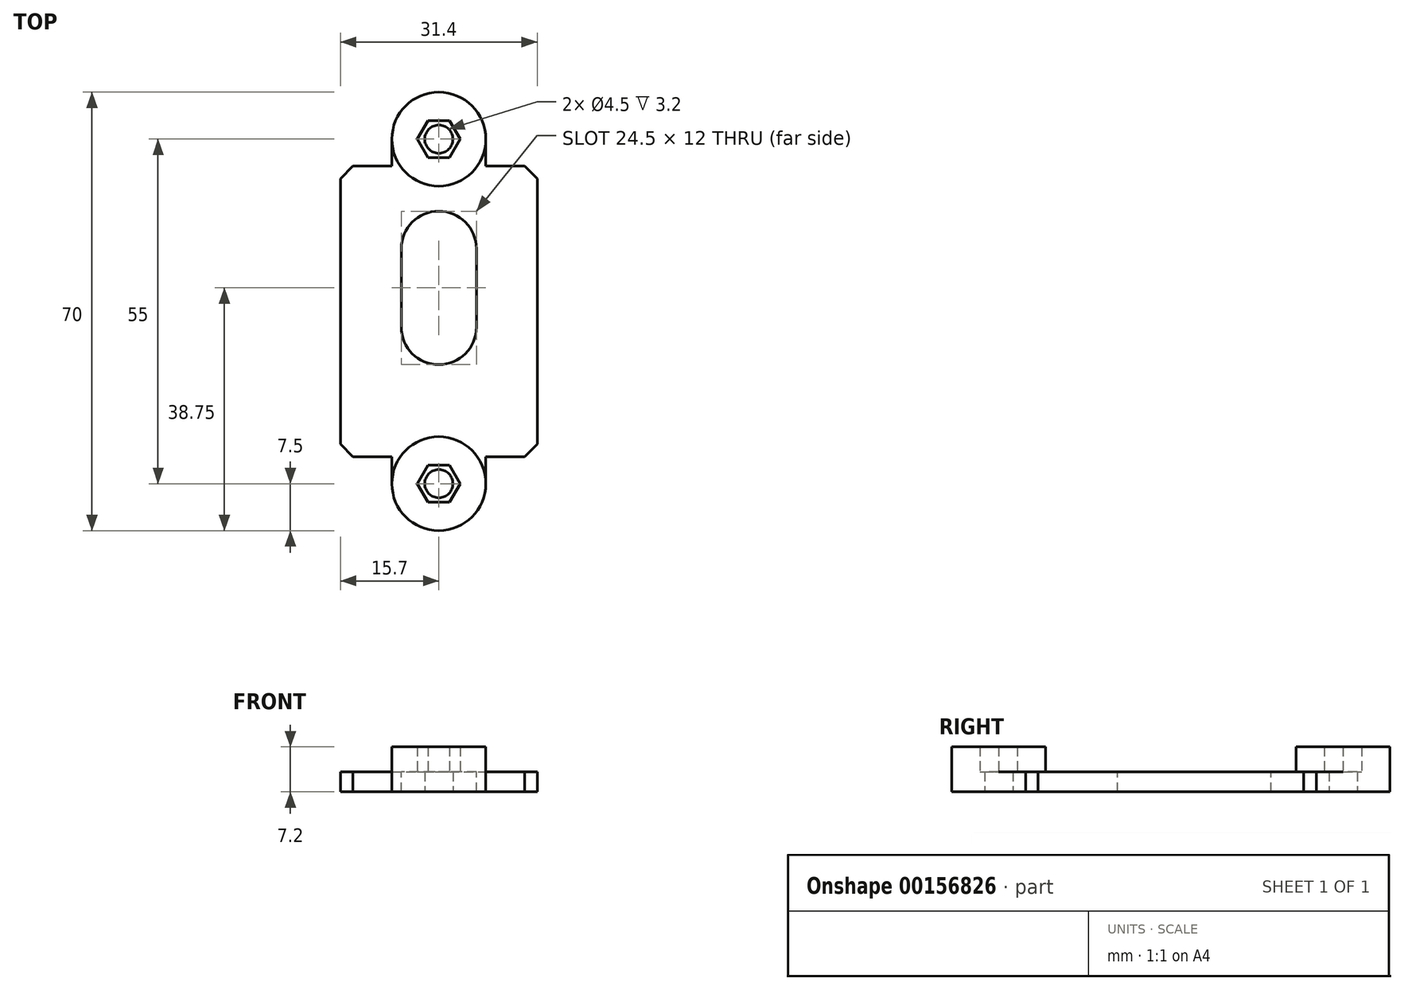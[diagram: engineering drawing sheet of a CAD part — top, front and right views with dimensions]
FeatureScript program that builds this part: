
annotation { "Feature Type Name" : "Feature", "Feature Type Description" : "" }
export const myFeature = defineFeature(function(context is Context, id is Id, definition is map)
    precondition{}
    {
        {
            var Q0;
            Q0=qCreatedBy(makeId("Top.planeOp"),FACE);
            var sketch = newSketch(context, id + "F0", { "sketchPlane" : qUnion([Q0])});
            skLineSegment(sketch, "E0.rect.bottom", {"start": v(12.5, -20) * mm, "end": v(-12.5, -20) * mm});
            skLineSegment(sketch, "E0.rect.top", {"start": v(12.5, 20) * mm, "end": v(-12.5, 20) * mm});
            skLineSegment(sketch, "E0.rect.left", {"start": v(12.5, -20) * mm, "end": v(12.5, 20) * mm});
            skLineSegment(sketch, "E0.rect.right", {"start": v(-12.5, -20) * mm, "end": v(-12.5, 20) * mm});
            skPoint(sketch, "E0.rect.middle", {"position": v(0, 0) * mm});
            skCircle(sketch, "E1", {"center": v(0, 0) * mm, "radius": 6.25 * mm});
            skSolve(sketch);
        }
        {
            var Q0;
            Q0=qSketchRegion(id+"F0",true);
            extrude(context, id + "F1", {"entities" : qUnion([Q0]), "depth" : 3.2 * mm});
        }
        {
            var Q0;
            Q0=makeQuery(id+"F1.opExtrude","CAP_FACE",FACE,{"disambiguationData":[OSD([sQuery(id+"F0.wireOp",EDGE,"E0.rect.bottom"),sQuery(id+"F0.wireOp",EDGE,"E0.rect.top"),sQuery(id+"F0.wireOp",EDGE,"E0.rect.left"),sQuery(id+"F0.wireOp",EDGE,"E0.rect.right"),sQuery(id+"F0.wireOp",EDGE,"E1")])],"isStart":false});
            var sketch = newSketch(context, id + "F2", { "sketchPlane" : qUnion([Q0])});
            skLineSegment(sketch, "E2.rect.bottom", {"start": v(12.5, 20) * mm, "end": v(-12.5, 20) * mm});
            skLineSegment(sketch, "E2.rect.top", {"start": v(12.5, -20) * mm, "end": v(-12.5, -20) * mm});
            skLineSegment(sketch, "E2.rect.left", {"start": v(12.5, 20) * mm, "end": v(12.5, -20) * mm});
            skLineSegment(sketch, "E2.rect.right", {"start": v(-12.5, 20) * mm, "end": v(-12.5, -20) * mm});
            skPoint(sketch, "E2.rect.middle", {"position": v(0, 0) * mm});
            skLineSegment(sketch, "E3.rect.bottom", {"start": v(15.7, 23.2) * mm, "end": v(7.5, 23.2) * mm});
            skLineSegment(sketch, "E3.rect.left", {"start": v(15.7, 23.2) * mm, "end": v(15.7, -23.2) * mm});
            skLineSegment(sketch, "E3.rect.right", {"start": v(-15.7, 23.2) * mm, "end": v(-15.7, -23.2) * mm});
            skLineSegment(sketch, "E4", {"start": v(-7.5, 23.2) * mm, "end": v(-7.5, 27.5) * mm});
            skLineSegment(sketch, "E5", {"start": v(0, 27.5) * mm, "end": v(0, 23.2) * mm, "construction": true});
            skLineSegment(sketch, "E6", {"start": v(0, 0) * mm, "end": v(-6.25, 0) * mm, "construction": true});
            skLineSegment(sketch, "E7.MirrorCS", {"start": v(7.5, 23.2) * mm, "end": v(7.5, 27.5) * mm});
            skArc(sketch, "E8", {"start": v(-7.5, 27.5) * mm, "mid": v(0, 35) * mm, "end": v(7.5, 27.5) * mm});
            skLineSegment(sketch, "E9.MirrorCS", {"start": v(-7.5, -23.2) * mm, "end": v(-7.5, -27.5) * mm});
            skLineSegment(sketch, "E10.MirrorCS", {"start": v(15.7, -23.2) * mm, "end": v(7.5, -23.2) * mm});
            skLineSegment(sketch, "E11.MirrorCS", {"start": v(0, -27.5) * mm, "end": v(0, -23.2) * mm, "construction": true});
            skArc(sketch, "E12.MirrorCS", {"start": v(-7.5, -27.5) * mm, "mid": v(0, -35) * mm, "end": v(7.5, -27.5) * mm});
            skLineSegment(sketch, "E13.MirrorCS", {"start": v(7.5, -23.2) * mm, "end": v(7.5, -27.5) * mm});
            skLineSegment(sketch, "E14.trimOffspring", {"start": v(-7.5, -23.2) * mm, "end": v(-15.7, -23.2) * mm});
            skLineSegment(sketch, "E15.trimOffspring", {"start": v(-7.5, 23.2) * mm, "end": v(-15.7, 23.2) * mm});
            skCircle(sketch, "E16.cCircle", {"center": v(0, 27.5) * mm, "radius": 2.98 * mm, "construction": true});
            skLineSegment(sketch, "E16.0", {"start": v(-1.72, 30.48) * mm, "end": v(1.72, 30.48) * mm});
            skLineSegment(sketch, "E16.1", {"start": v(1.72, 30.48) * mm, "end": v(3.44, 27.5) * mm});
            skLineSegment(sketch, "E16.2", {"start": v(3.44, 27.5) * mm, "end": v(1.72, 24.52) * mm});
            skLineSegment(sketch, "E16.3", {"start": v(1.72, 24.52) * mm, "end": v(-1.72, 24.52) * mm});
            skLineSegment(sketch, "E16.4", {"start": v(-1.72, 24.52) * mm, "end": v(-3.44, 27.5) * mm});
            skLineSegment(sketch, "E16.5", {"start": v(-3.44, 27.5) * mm, "end": v(-1.72, 30.48) * mm});
            skPoint(sketch, "E16.0.midPoint", {"position": v(0, 30.48) * mm});
            skCircle(sketch, "E17.cCircle", {"center": v(0, -27.5) * mm, "radius": 2.98 * mm, "construction": true});
            skLineSegment(sketch, "E17.0", {"start": v(-1.72, -24.52) * mm, "end": v(1.72, -24.52) * mm});
            skLineSegment(sketch, "E17.1", {"start": v(1.72, -24.52) * mm, "end": v(3.44, -27.5) * mm});
            skLineSegment(sketch, "E17.2", {"start": v(3.44, -27.5) * mm, "end": v(1.72, -30.47) * mm});
            skLineSegment(sketch, "E17.3", {"start": v(1.72, -30.48) * mm, "end": v(-1.72, -30.48) * mm});
            skLineSegment(sketch, "E17.4", {"start": v(-1.72, -30.48) * mm, "end": v(-3.44, -27.5) * mm});
            skLineSegment(sketch, "E17.5", {"start": v(-3.44, -27.5) * mm, "end": v(-1.72, -24.52) * mm});
            skPoint(sketch, "E17.0.midPoint", {"position": v(0, -24.52) * mm});
            skSolve(sketch);
        }
        {
            var Q0;
            Q0=qSketchRegion(id+"F2",true);
            extrude(context, id + "F3", {"entities" : qUnion([Q0]), "operationType" : NewBodyOperationType.ADD, "oppositeDirection" : true, "depth" : 40 * mm});
        }
        {
            var Q0;
            Q0=makeQuery(id+"F3.boolean.opBoolean","MERGE",FACE,{"derivedFrom":[makeQuery(id+"F1.opExtrude","CAP_FACE",FACE,{"disambiguationData":[OSD([sQuery(id+"F0.wireOp",EDGE,"E0.rect.bottom"),sQuery(id+"F0.wireOp",EDGE,"E0.rect.top"),sQuery(id+"F0.wireOp",EDGE,"E0.rect.left"),sQuery(id+"F0.wireOp",EDGE,"E0.rect.right"),sQuery(id+"F0.wireOp",EDGE,"E1")])],"isStart":false}),makeQuery(id+"F3.opExtrude","CAP_FACE",FACE,{"disambiguationData":[OSD([sQuery(id+"F2.wireOp",EDGE,"E2.rect.bottom"),sQuery(id+"F2.wireOp",EDGE,"E2.rect.top"),sQuery(id+"F2.wireOp",EDGE,"E2.rect.left"),sQuery(id+"F2.wireOp",EDGE,"E2.rect.right"),sQuery(id+"F2.wireOp",EDGE,"E3.rect.bottom"),sQuery(id+"F2.wireOp",EDGE,"E3.rect.top"),sQuery(id+"F2.wireOp",EDGE,"E3.rect.left"),sQuery(id+"F2.wireOp",EDGE,"E3.rect.right")])],"isStart":true})]});
            var sketch = newSketch(context, id + "F4", { "sketchPlane" : qUnion([Q0])});
            skLineSegment(sketch, "E18", {"start": v(-15.7, 23.2) * mm, "end": v(-30.7, 23.2) * mm});
            skLineSegment(sketch, "E19", {"start": v(-30.7, 23.2) * mm, "end": v(-30.7, -23.2) * mm});
            skLineSegment(sketch, "E20", {"start": v(-30.7, -23.2) * mm, "end": v(-15.7, -23.2) * mm});
            skLineSegment(sketch, "E21", {"start": v(-15.7, -23.2) * mm, "end": v(-15.7, 23.2) * mm});
            skCircle(sketch, "E22", {"center": v(-23.2, 13.2) * mm, "radius": 2.25 * mm});
            skCircle(sketch, "E23", {"center": v(-23.2, -13.2) * mm, "radius": 2.25 * mm});
            skPoint(sketch, "E23.centerSnap0", {"position": v(-23.2, -23.2) * mm});
            skSolve(sketch);
        }
        {
            var Q0;
            Q0=qSketchRegion(id+"F4",true);
            extrude(context, id + "F5", {"entities" : qUnion([Q0]), "operationType" : NewBodyOperationType.ADD, "oppositeDirection" : true, "depth" : 5 * mm});
        }
        {
            var Q0;
            Q0=makeQuery(id+"F3.opExtrude","SWEPT_EDGE",EDGE,{"disambiguationData":[OSD([sQuery(id+"F2.wireOp",EDGE,"E3.rect.bottom"),sQuery(id+"F2.wireOp",EDGE,"E3.rect.left")])]});
            var Q1;
            Q1=makeQuery(id+"F3.opExtrude","SWEPT_EDGE",EDGE,{"disambiguationData":[OSD([sQuery(id+"F2.wireOp",EDGE,"E3.rect.right"),sQuery(id+"F2.wireOp",EDGE,"E15.trimOffspring")])]});
            var Q2;
            Q2=makeQuery(id+"F3.opExtrude","SWEPT_EDGE",EDGE,{"disambiguationData":[OSD([sQuery(id+"F2.wireOp",EDGE,"E3.rect.right"),sQuery(id+"F2.wireOp",EDGE,"E14.trimOffspring")])]});
            var Q3;
            Q3=makeQuery(id+"F3.opExtrude","SWEPT_EDGE",EDGE,{"disambiguationData":[OSD([sQuery(id+"F2.wireOp",EDGE,"E3.rect.bottom"),sQuery(id+"F2.wireOp",EDGE,"E3.rect.left")])]});
            var Q4;
            Q4=makeQuery(id+"F3.opExtrude","SWEPT_EDGE",EDGE,{"disambiguationData":[OSD([sQuery(id+"F2.wireOp",EDGE,"E3.rect.bottom"),sQuery(id+"F2.wireOp",EDGE,"E3.rect.left")])]});
            var Q5;
            Q5=makeQuery(id+"F3.opExtrude","SWEPT_EDGE",EDGE,{"disambiguationData":[OSD([sQuery(id+"F2.wireOp",EDGE,"E3.rect.left"),sQuery(id+"F2.wireOp",EDGE,"E10.MirrorCS")])]});
            var Q6;
            Q6=makeQuery(id+"F3.opExtrude","SWEPT_EDGE",EDGE,{"disambiguationData":[OSD([sQuery(id+"F2.wireOp",EDGE,"E3.rect.right"),sQuery(id+"F2.wireOp",EDGE,"E15.trimOffspring")])]});
            var Q7;
            Q7=makeQuery(id+"F3.opExtrude","SWEPT_EDGE",EDGE,{"disambiguationData":[OSD([sQuery(id+"F2.wireOp",EDGE,"E3.rect.right"),sQuery(id+"F2.wireOp",EDGE,"E14.trimOffspring")])]});
            var Q8;
            Q8=makeQuery(id+"F5.opExtrude","SWEPT_EDGE",EDGE,{"disambiguationData":[OSD([sQuery(id+"F4.wireOp",EDGE,"E18"),sQuery(id+"F4.wireOp",EDGE,"E19")])]});
            var Q9;
            Q9=makeQuery(id+"F5.opExtrude","SWEPT_EDGE",EDGE,{"disambiguationData":[OSD([sQuery(id+"F4.wireOp",EDGE,"E19"),sQuery(id+"F4.wireOp",EDGE,"E20")])]});
            chamfer(context, id + "F6", {"entities" : qUnion([Q0, Q1, Q2, Q3, Q4, Q5, Q6, Q7, Q8, Q9]), "width" : 2 * mm, "tangentPropagation" : true});
        }
        {
            var Q0;
            Q0=makeQuery(id+"F3.opExtrude","CAP_FACE",FACE,{"disambiguationData":[OSD([sQuery(id+"F2.wireOp",EDGE,"E2.rect.bottom"),sQuery(id+"F2.wireOp",EDGE,"E2.rect.top"),sQuery(id+"F2.wireOp",EDGE,"E2.rect.left"),sQuery(id+"F2.wireOp",EDGE,"E2.rect.right"),sQuery(id+"F2.wireOp",EDGE,"E3.rect.bottom"),sQuery(id+"F2.wireOp",EDGE,"E3.rect.left"),sQuery(id+"F2.wireOp",EDGE,"E3.rect.right"),sQuery(id+"F2.wireOp",EDGE,"E4"),sQuery(id+"F2.wireOp",EDGE,"E7.MirrorCS"),sQuery(id+"F2.wireOp",EDGE,"E8"),sQuery(id+"F2.wireOp",EDGE,"E9.MirrorCS"),sQuery(id+"F2.wireOp",EDGE,"E10.MirrorCS"),sQuery(id+"F2.wireOp",EDGE,"E12.MirrorCS"),sQuery(id+"F2.wireOp",EDGE,"E13.MirrorCS"),sQuery(id+"F2.wireOp",EDGE,"E14.trimOffspring"),sQuery(id+"F2.wireOp",EDGE,"E15.trimOffspring"),sQuery(id+"F2.wireOp",EDGE,"E16.0"),sQuery(id+"F2.wireOp",EDGE,"E16.1"),sQuery(id+"F2.wireOp",EDGE,"E16.2"),sQuery(id+"F2.wireOp",EDGE,"E16.3"),sQuery(id+"F2.wireOp",EDGE,"E16.4"),sQuery(id+"F2.wireOp",EDGE,"E16.5"),sQuery(id+"F2.wireOp",EDGE,"E17.0"),sQuery(id+"F2.wireOp",EDGE,"E17.1"),sQuery(id+"F2.wireOp",EDGE,"E17.2"),sQuery(id+"F2.wireOp",EDGE,"E17.3"),sQuery(id+"F2.wireOp",EDGE,"E17.4"),sQuery(id+"F2.wireOp",EDGE,"E17.5")])],"isStart":false});
            var sketch = newSketch(context, id + "F7", { "sketchPlane" : qUnion([Q0])});
            skCircle(sketch, "E24.cCircle", {"center": v(0, 27.5) * mm, "radius": 2.98 * mm, "construction": true});
            skLineSegment(sketch, "E24.0", {"start": v(-1.72, 30.48) * mm, "end": v(1.72, 30.47) * mm});
            skLineSegment(sketch, "E24.1", {"start": v(1.72, 30.47) * mm, "end": v(3.44, 27.5) * mm});
            skLineSegment(sketch, "E24.2", {"start": v(3.44, 27.5) * mm, "end": v(1.72, 24.52) * mm});
            skLineSegment(sketch, "E24.3", {"start": v(1.72, 24.52) * mm, "end": v(-1.72, 24.53) * mm});
            skLineSegment(sketch, "E24.4", {"start": v(-1.72, 24.53) * mm, "end": v(-3.44, 27.5) * mm});
            skLineSegment(sketch, "E24.5", {"start": v(-3.44, 27.5) * mm, "end": v(-1.72, 30.48) * mm});
            skPoint(sketch, "E24.0.midPoint", {"position": v(0, 30.48) * mm});
            skLineSegment(sketch, "E25", {"start": v(0, 0) * mm, "end": v(12.5, 0) * mm, "construction": true});
            skCircle(sketch, "E26", {"center": v(0, 27.5) * mm, "radius": 2.25 * mm});
            skLineSegment(sketch, "E27.MirrorCS", {"start": v(-1.72, -30.48) * mm, "end": v(1.72, -30.47) * mm});
            skCircle(sketch, "E28.MirrorC", {"center": v(0, -27.5) * mm, "radius": 2.98 * mm, "construction": true});
            skLineSegment(sketch, "E29.MirrorCS", {"start": v(1.72, -30.47) * mm, "end": v(3.44, -27.5) * mm});
            skLineSegment(sketch, "E30.MirrorCS", {"start": v(3.44, -27.5) * mm, "end": v(1.72, -24.52) * mm});
            skLineSegment(sketch, "E31.MirrorCS", {"start": v(1.72, -24.52) * mm, "end": v(-1.72, -24.53) * mm});
            skLineSegment(sketch, "E32.MirrorCS", {"start": v(-1.72, -24.53) * mm, "end": v(-3.44, -27.5) * mm});
            skLineSegment(sketch, "E33.MirrorCS", {"start": v(-3.44, -27.5) * mm, "end": v(-1.72, -30.48) * mm});
            skCircle(sketch, "E34.MirrorC", {"center": v(0, -27.5) * mm, "radius": 2.25 * mm});
            skPoint(sketch, "E35.MirrorP", {"position": v(0, -30.48) * mm});
            skSolve(sketch);
        }
        {
            var Q0;
            Q0=qSketchRegion(id+"F7",true);
            extrude(context, id + "F8", {"entities" : qUnion([Q0]), "operationType" : NewBodyOperationType.ADD, "oppositeDirection" : true, "depth" : 3.2 * mm});
        }
        {
            var Q0;
            Q0=makeQuery(id+"F5.boolean.opBoolean","MERGE",FACE,{"derivedFrom":[makeQuery(id+"F3.boolean.opBoolean","MERGE",FACE,{"derivedFrom":[makeQuery(id+"F1.opExtrude","CAP_FACE",FACE,{"disambiguationData":[OSD([sQuery(id+"F0.wireOp",EDGE,"E0.rect.bottom"),sQuery(id+"F0.wireOp",EDGE,"E0.rect.top"),sQuery(id+"F0.wireOp",EDGE,"E0.rect.left"),sQuery(id+"F0.wireOp",EDGE,"E0.rect.right"),sQuery(id+"F0.wireOp",EDGE,"E1")])],"isStart":false}),makeQuery(id+"F3.opExtrude","CAP_FACE",FACE,{"disambiguationData":[OSD([sQuery(id+"F2.wireOp",EDGE,"E2.rect.bottom"),sQuery(id+"F2.wireOp",EDGE,"E2.rect.top"),sQuery(id+"F2.wireOp",EDGE,"E2.rect.left"),sQuery(id+"F2.wireOp",EDGE,"E2.rect.right"),sQuery(id+"F2.wireOp",EDGE,"E3.rect.bottom"),sQuery(id+"F2.wireOp",EDGE,"E3.rect.left"),sQuery(id+"F2.wireOp",EDGE,"E3.rect.right"),sQuery(id+"F2.wireOp",EDGE,"E4"),sQuery(id+"F2.wireOp",EDGE,"E7.MirrorCS"),sQuery(id+"F2.wireOp",EDGE,"E8"),sQuery(id+"F2.wireOp",EDGE,"E9.MirrorCS"),sQuery(id+"F2.wireOp",EDGE,"E10.MirrorCS"),sQuery(id+"F2.wireOp",EDGE,"E12.MirrorCS"),sQuery(id+"F2.wireOp",EDGE,"E13.MirrorCS"),sQuery(id+"F2.wireOp",EDGE,"E14.trimOffspring"),sQuery(id+"F2.wireOp",EDGE,"E15.trimOffspring"),sQuery(id+"F2.wireOp",EDGE,"E16.0"),sQuery(id+"F2.wireOp",EDGE,"E16.1"),sQuery(id+"F2.wireOp",EDGE,"E16.2"),sQuery(id+"F2.wireOp",EDGE,"E16.3"),sQuery(id+"F2.wireOp",EDGE,"E16.4"),sQuery(id+"F2.wireOp",EDGE,"E16.5"),sQuery(id+"F2.wireOp",EDGE,"E17.0"),sQuery(id+"F2.wireOp",EDGE,"E17.1"),sQuery(id+"F2.wireOp",EDGE,"E17.2"),sQuery(id+"F2.wireOp",EDGE,"E17.3"),sQuery(id+"F2.wireOp",EDGE,"E17.4"),sQuery(id+"F2.wireOp",EDGE,"E17.5")])],"isStart":true})]}),makeQuery(id+"F5.opExtrude","CAP_FACE",FACE,{"disambiguationData":[OSD([sQuery(id+"F4.wireOp",EDGE,"E18"),sQuery(id+"F4.wireOp",EDGE,"E19"),sQuery(id+"F4.wireOp",EDGE,"E20"),sQuery(id+"F4.wireOp",EDGE,"E21"),sQuery(id+"F4.wireOp",EDGE,"E22"),sQuery(id+"F4.wireOp",EDGE,"E23")])],"isStart":true})]});
            var sketch = newSketch(context, id + "F9", { "sketchPlane" : qUnion([Q0])});
            skLineSegment(sketch, "E36.rect.bottom", {"start": v(15.7, -35) * mm, "end": v(-30.7, -35) * mm});
            skLineSegment(sketch, "E36.rect.top", {"start": v(15.7, 35) * mm, "end": v(-30.7, 35) * mm});
            skLineSegment(sketch, "E36.rect.left", {"start": v(15.7, -35) * mm, "end": v(15.7, 35) * mm});
            skLineSegment(sketch, "E36.rect.right", {"start": v(-30.7, -35) * mm, "end": v(-30.7, 35) * mm});
            skPoint(sketch, "E36.rect.middle", {"position": v(-7.5, 0) * mm});
            skSolve(sketch);
        }
        {
            var Q0;
            Q0=qSketchRegion(id+"F9",true);
            extrude(context, id + "F10", {"entities" : qUnion([Q0]), "operationType" : NewBodyOperationType.REMOVE, "oppositeDirection" : true, "depth" : 36.8 * mm});
        }
        {
            var Q0;
            Q0=makeQuery(id+"F10.boolean.opBoolean","MERGE",FACE,{"derivedFrom":[makeQuery(id+"F8.opExtrude","CAP_FACE",FACE,{"disambiguationData":[OSD([sQuery(id+"F7.wireOp",EDGE,"E24.0"),sQuery(id+"F7.wireOp",EDGE,"E24.1"),sQuery(id+"F7.wireOp",EDGE,"E24.2"),sQuery(id+"F7.wireOp",EDGE,"E24.3"),sQuery(id+"F7.wireOp",EDGE,"E24.4"),sQuery(id+"F7.wireOp",EDGE,"E24.5"),sQuery(id+"F7.wireOp",EDGE,"E26")])],"isStart":false}),makeQuery(id+"F8.opExtrude","CAP_FACE",FACE,{"disambiguationData":[OSD([sQuery(id+"F7.wireOp",EDGE,"E27.MirrorCS"),sQuery(id+"F7.wireOp",EDGE,"E29.MirrorCS"),sQuery(id+"F7.wireOp",EDGE,"E30.MirrorCS"),sQuery(id+"F7.wireOp",EDGE,"E31.MirrorCS"),sQuery(id+"F7.wireOp",EDGE,"E32.MirrorCS"),sQuery(id+"F7.wireOp",EDGE,"E33.MirrorCS"),sQuery(id+"F7.wireOp",EDGE,"E34.MirrorC")])],"isStart":false}),makeQuery(id+"F10.opExtrude","CAP_FACE",FACE,{"disambiguationData":[OSD([sQuery(id+"F9.wireOp",EDGE,"E36.rect.bottom"),sQuery(id+"F9.wireOp",EDGE,"E36.rect.top"),sQuery(id+"F9.wireOp",EDGE,"E36.rect.left"),sQuery(id+"F9.wireOp",EDGE,"E36.rect.right")])],"isStart":false})]});
            var sketch = newSketch(context, id + "F11", { "sketchPlane" : qUnion([Q0])});
            skLineSegment(sketch, "E37.rect.bottom", {"start": v(12.5, 20) * mm, "end": v(-12.5, 20) * mm});
            skLineSegment(sketch, "E37.rect.top", {"start": v(12.5, -20) * mm, "end": v(-12.5, -20) * mm});
            skLineSegment(sketch, "E37.rect.left", {"start": v(12.5, 20) * mm, "end": v(12.5, -20) * mm});
            skLineSegment(sketch, "E37.rect.right", {"start": v(-12.5, 20) * mm, "end": v(-12.5, -20) * mm});
            skPoint(sketch, "E37.rect.middle", {"position": v(0, 0) * mm});
            skArc(sketch, "E38", {"start": v(6, 10) * mm, "mid": v(0, 16) * mm, "end": v(-6, 10) * mm});
            skArc(sketch, "E39", {"start": v(-6, -2.5) * mm, "mid": v(0, -8.5) * mm, "end": v(6, -2.5) * mm});
            skLineSegment(sketch, "E40", {"start": v(6, 10) * mm, "end": v(6, -2.5) * mm});
            skLineSegment(sketch, "E41", {"start": v(-6, 10) * mm, "end": v(-6, -2.5) * mm});
            skSolve(sketch);
        }
        {
            var Q0;
            Q0=qSketchRegion(id+"F11",true);
            extrude(context, id + "F12", {"entities" : qUnion([Q0]), "operationType" : NewBodyOperationType.ADD, "oppositeDirection" : true, "depth" : 3.2 * mm});
        }
        {
            var Q0;
            Q0=makeQuery(id+"F12.boolean.opBoolean","MERGE",FACE,{"derivedFrom":[makeQuery(id+"F10.boolean.opBoolean","MERGE",FACE,{"derivedFrom":[makeQuery(id+"F8.opExtrude","CAP_FACE",FACE,{"disambiguationData":[OSD([sQuery(id+"F7.wireOp",EDGE,"E24.0"),sQuery(id+"F7.wireOp",EDGE,"E24.1"),sQuery(id+"F7.wireOp",EDGE,"E24.2"),sQuery(id+"F7.wireOp",EDGE,"E24.3"),sQuery(id+"F7.wireOp",EDGE,"E24.4"),sQuery(id+"F7.wireOp",EDGE,"E24.5"),sQuery(id+"F7.wireOp",EDGE,"E26")])],"isStart":false}),makeQuery(id+"F8.opExtrude","CAP_FACE",FACE,{"disambiguationData":[OSD([sQuery(id+"F7.wireOp",EDGE,"E27.MirrorCS"),sQuery(id+"F7.wireOp",EDGE,"E29.MirrorCS"),sQuery(id+"F7.wireOp",EDGE,"E30.MirrorCS"),sQuery(id+"F7.wireOp",EDGE,"E31.MirrorCS"),sQuery(id+"F7.wireOp",EDGE,"E32.MirrorCS"),sQuery(id+"F7.wireOp",EDGE,"E33.MirrorCS"),sQuery(id+"F7.wireOp",EDGE,"E34.MirrorC")])],"isStart":false}),makeQuery(id+"F10.opExtrude","CAP_FACE",FACE,{"disambiguationData":[OSD([sQuery(id+"F9.wireOp",EDGE,"E36.rect.bottom"),sQuery(id+"F9.wireOp",EDGE,"E36.rect.top"),sQuery(id+"F9.wireOp",EDGE,"E36.rect.left"),sQuery(id+"F9.wireOp",EDGE,"E36.rect.right")])],"isStart":false})]}),makeQuery(id+"F12.opExtrude","CAP_FACE",FACE,{"disambiguationData":[OSD([sQuery(id+"F11.wireOp",EDGE,"E37.rect.bottom"),sQuery(id+"F11.wireOp",EDGE,"E37.rect.top"),sQuery(id+"F11.wireOp",EDGE,"E37.rect.left"),sQuery(id+"F11.wireOp",EDGE,"E37.rect.right"),sQuery(id+"F11.wireOp",EDGE,"e01bcde1-b1cc-4272-b2a3-0804ea6b9ef7"),sQuery(id+"F11.wireOp",EDGE,"fe11aa55-1cf9-4a09-b6d3-55c628399e40")])],"isStart":true})]});
            var sketch = newSketch(context, id + "F13", { "sketchPlane" : qUnion([Q0])});
            skCircle(sketch, "E42.cCircle", {"center": v(0, 27.5) * mm, "radius": 2.98 * mm, "construction": true});
            skLineSegment(sketch, "E42.0", {"start": v(-1.72, 30.48) * mm, "end": v(1.72, 30.48) * mm});
            skLineSegment(sketch, "E42.1", {"start": v(1.72, 30.48) * mm, "end": v(3.44, 27.5) * mm});
            skLineSegment(sketch, "E42.2", {"start": v(3.44, 27.5) * mm, "end": v(1.72, 24.53) * mm});
            skLineSegment(sketch, "E42.3", {"start": v(1.72, 24.52) * mm, "end": v(-1.72, 24.52) * mm});
            skLineSegment(sketch, "E42.4", {"start": v(-1.72, 24.52) * mm, "end": v(-3.44, 27.5) * mm});
            skLineSegment(sketch, "E42.5", {"start": v(-3.44, 27.5) * mm, "end": v(-1.72, 30.47) * mm});
            skPoint(sketch, "E42.0.midPoint", {"position": v(0, 30.48) * mm});
            skCircle(sketch, "E43.cCircle", {"center": v(0, -27.5) * mm, "radius": 2.98 * mm, "construction": true});
            skLineSegment(sketch, "E43.0", {"start": v(-1.72, -24.52) * mm, "end": v(1.72, -24.52) * mm});
            skLineSegment(sketch, "E43.1", {"start": v(1.72, -24.53) * mm, "end": v(3.44, -27.5) * mm});
            skLineSegment(sketch, "E43.2", {"start": v(3.44, -27.5) * mm, "end": v(1.72, -30.47) * mm});
            skLineSegment(sketch, "E43.3", {"start": v(1.72, -30.48) * mm, "end": v(-1.72, -30.48) * mm});
            skLineSegment(sketch, "E43.4", {"start": v(-1.72, -30.48) * mm, "end": v(-3.44, -27.5) * mm});
            skLineSegment(sketch, "E43.5", {"start": v(-3.44, -27.5) * mm, "end": v(-1.72, -24.52) * mm});
            skPoint(sketch, "E43.0.midPoint", {"position": v(0, -24.52) * mm});
            skCircle(sketch, "E44", {"center": v(0, 27.5) * mm, "radius": 7.5 * mm});
            skCircle(sketch, "E45", {"center": v(0, -27.5) * mm, "radius": 7.5 * mm});
            skSolve(sketch);
        }
        {
            var Q0;
            Q0=qSketchRegion(id+"F13",true);
            extrude(context, id + "F14", {"entities" : qUnion([Q0]), "operationType" : NewBodyOperationType.ADD, "depth" : 4 * mm});
        }
    });
